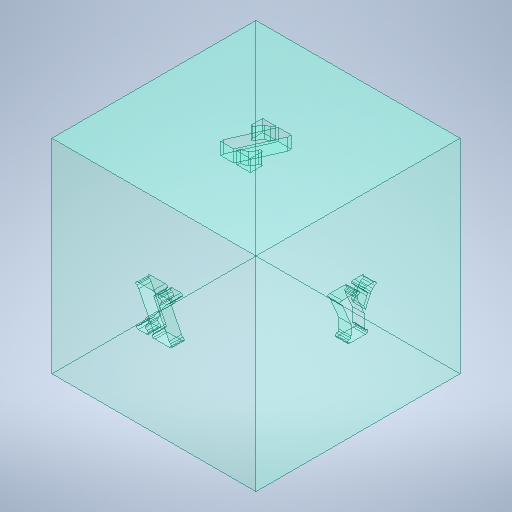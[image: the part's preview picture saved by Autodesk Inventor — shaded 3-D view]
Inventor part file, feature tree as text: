
AUTODESK INVENTOR PART (.ipt)
format: ipt  version: 2025.2 (Build 292293000, 293)  size: 913,408 bytes
history: native  units: mm
features: extrude x4, sketch x4, other x1
ambient origin geometry x8: Origin, YZ Plane, XZ Plane, XY Plane, X Axis, Y Axis, Z Axis, Center Point
bodies: Body1 (feature_tree)
feature tree (9):
  other  "Sólido1"
  extrude  "Extrusão1"  Depth=50.0mm
  extrude  "Extrusão2"  Depth=9.123264mm
  extrude  "Extrusão3"  Depth=3.0mm TaperAngle=0.0deg
  extrude  "Extrusão4"  Depth=10.0mm
  sketch  "Esboço1"  dims[d0=50.0mm d1=50.0mm]
  sketch  "Esboço2"  dims[d2=0.0mm d3=9.123264mm]
  sketch  "Esboço3"  dims[d4=10.0mm d5=3.0mm d6=0.0mm]
  sketch  "Esboço4"  dims[d7=8.958333mm d8=10.0mm d9=3.0mm d10=0.0mm d11=7.855903mm d12=10.0mm d13=3.0mm d14=0.0mm]
